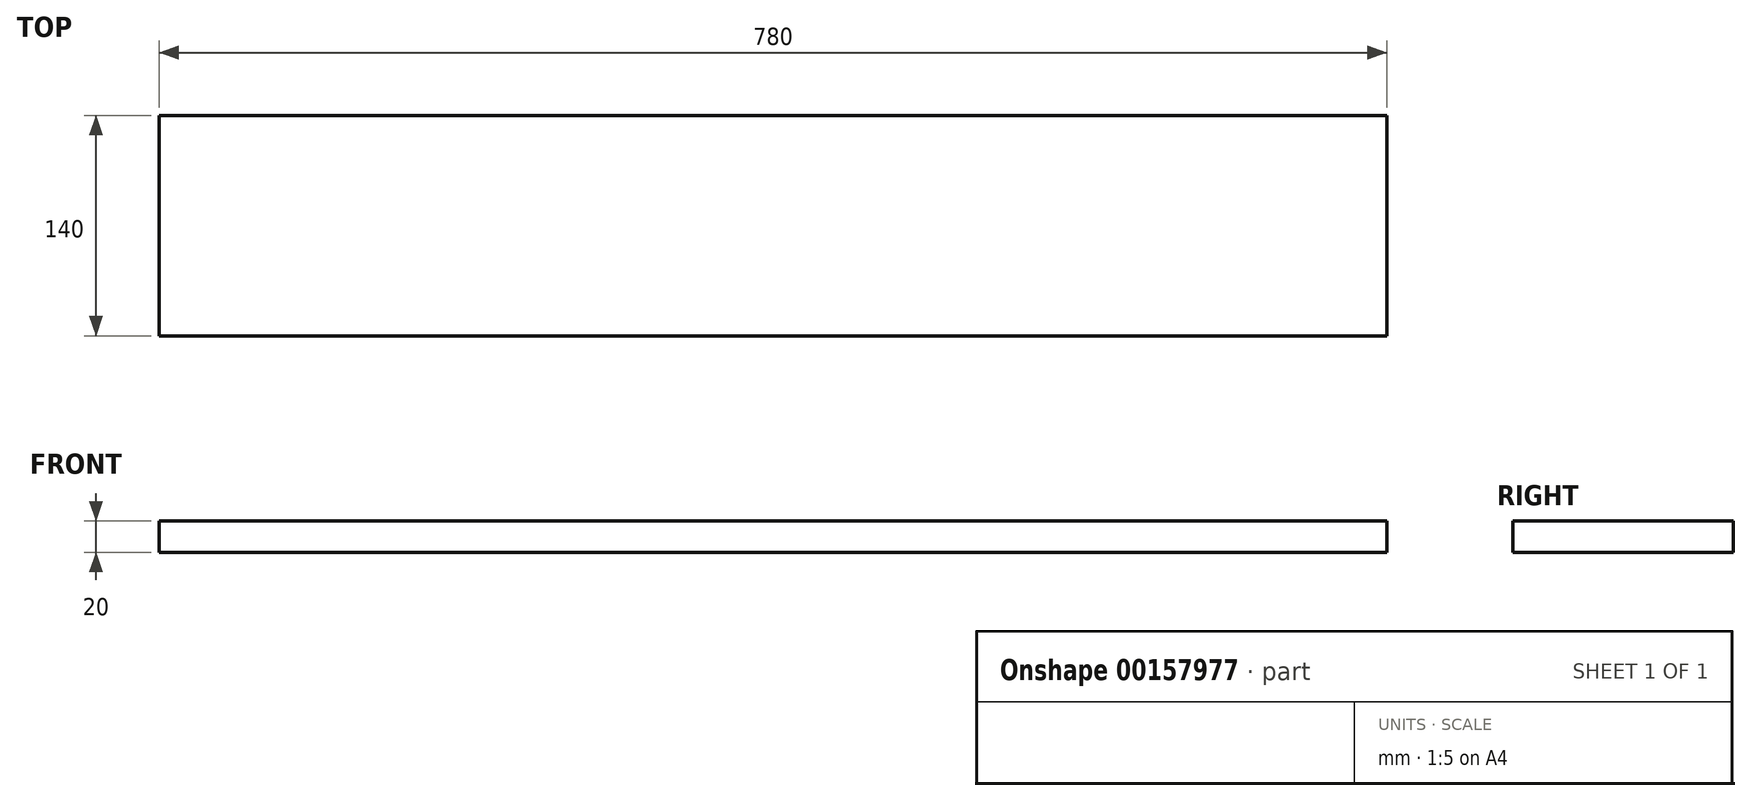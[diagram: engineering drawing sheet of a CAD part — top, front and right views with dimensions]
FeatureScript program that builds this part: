
annotation { "Feature Type Name" : "Feature", "Feature Type Description" : "" }
export const myFeature = defineFeature(function(context is Context, id is Id, definition is map)
    precondition{}
    {
        {
            var Q0;
            Q0=qCreatedBy(makeId("Top.planeOp"),FACE);
            var sketch = newSketch(context, id + "F0", { "sketchPlane" : qUnion([Q0])});
            skLineSegment(sketch, "E0.bottom", {"start": v(-390, -70) * mm, "end": v(390, -70) * mm});
            skLineSegment(sketch, "E0.top", {"start": v(-390, 70) * mm, "end": v(390, 70) * mm});
            skLineSegment(sketch, "E0.left", {"start": v(-390, -70) * mm, "end": v(-390, 70) * mm});
            skLineSegment(sketch, "E0.right", {"start": v(390, -70) * mm, "end": v(390, 70) * mm});
            skPoint(sketch, "E0.middle", {"position": v(0, 0) * mm});
            skSolve(sketch);
        }
        {
            var Q0;
            Q0=qSketchRegion(id+"F0",true);
            extrude(context, id + "F1", {"entities" : qUnion([Q0]), "endBound" : BoundingType.SYMMETRIC, "depth" : 20 * mm});
        }
    });
